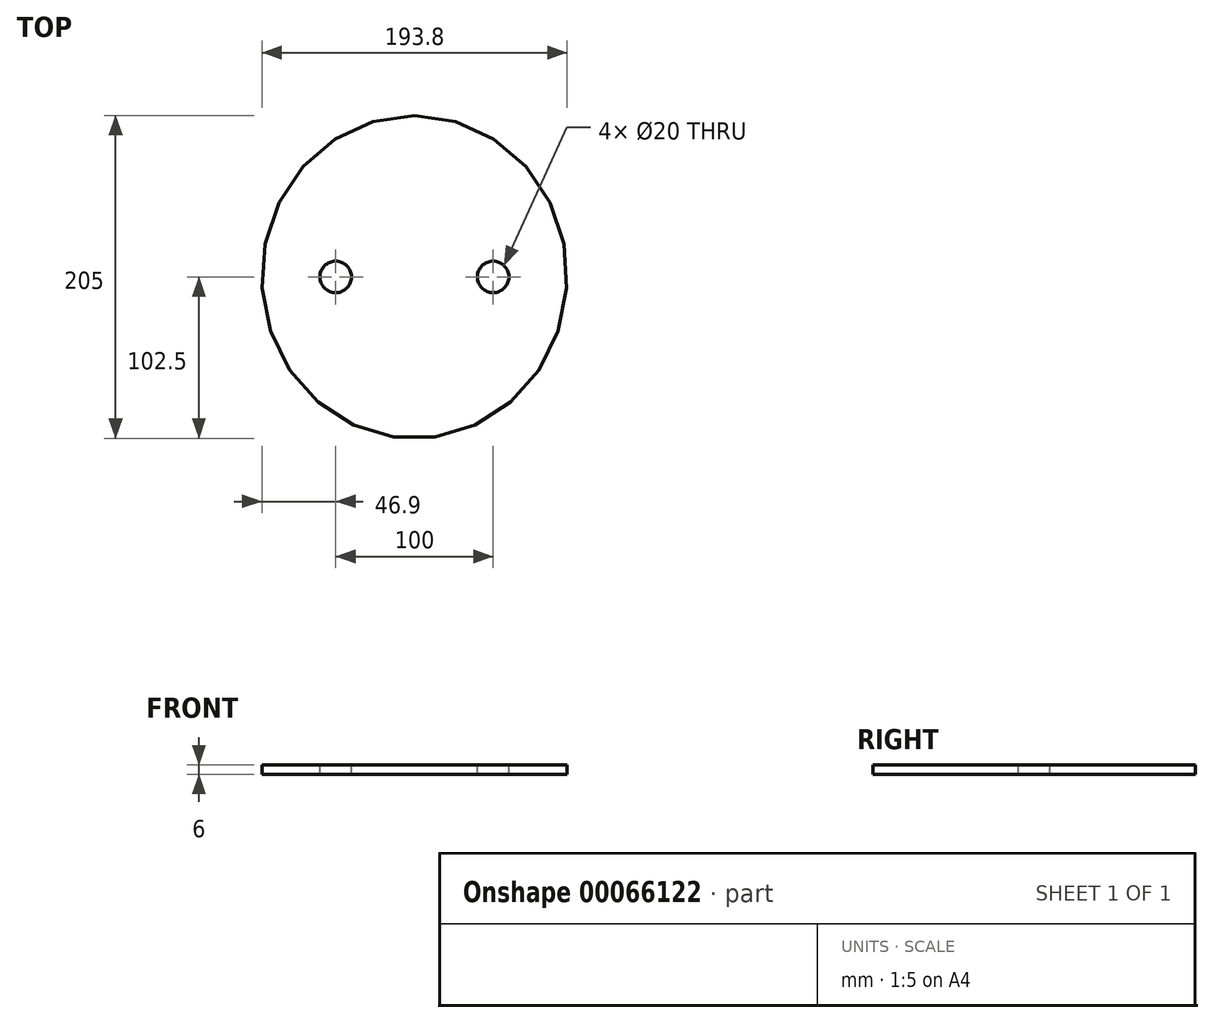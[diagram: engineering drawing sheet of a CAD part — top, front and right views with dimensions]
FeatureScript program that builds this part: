
annotation { "Feature Type Name" : "Feature", "Feature Type Description" : "" }
export const myFeature = defineFeature(function(context is Context, id is Id, definition is map)
    precondition{}
    {
        {
            var Q0;
            Q0=qCreatedBy(makeId("Top.planeOp"),FACE);
            var sketch = newSketch(context, id + "F0", { "sketchPlane" : qUnion([Q0])});
            skEllipse(sketch, "E0", {"center": v(0, 0) * mm, "majorRadius": 102.5 * mm, "minorRadius": 96.9 * mm, "majorAxis": v(0, 1)});
            skLineSegment(sketch, "E1", {"start": v(0, 102.5) * mm, "end": v(0, -102.5) * mm, "construction": true});
            skLineSegment(sketch, "E2", {"start": v(-96.9, 0) * mm, "end": v(96.9, 0) * mm, "construction": true});
            skSolve(sketch);
        }
        {
            var Q0;
            Q0=makeQuery(id+"F0.imprint","IMPRINT",FACE,{"disambiguationData":[TD([[makeQuery(id+"F0.imprint","IMPRINT",EDGE,{"derivedFrom":sQuery(id+"F0.wireOp",EDGE,"E0")}),1.0]])]});
            extrude(context, id + "F1", {"entities" : qUnion([Q0]), "depth" : 6 * mm});
        }
        {
            var Q0;
            Q0=makeQuery(id+"F1.opExtrude","CAP_FACE",FACE,{"disambiguationData":[OSD([sQuery(id+"F0.wireOp",EDGE,"E0")])],"isStart":false});
            var sketch = newSketch(context, id + "F2", { "sketchPlane" : qUnion([Q0])});
            skPoint(sketch, "E3", {"position": v(-50, 0) * mm});
            skPoint(sketch, "E4", {"position": v(50, 0) * mm});
            skSolve(sketch);
        }
        {
            var Q0;
            Q0=sQuery(id+"F2.wireOp",VERTEX,"E3");
            var Q1;
            Q1=sQuery(id+"F2.wireOp",VERTEX,"E4");
            var Q2;
            Q2=makeQuery(id+"F1.opExtrude","SWEPT_BODY",BODY,{"disambiguationData":[OSD([sQuery(id+"F0.wireOp",EDGE,"E0")])]});
            hole(context, id + "F3", {"style" : HoleStyle.SIMPLE, "holeDiameter" : 20 * mm, "endStyle" : HoleEndStyle.THROUGH, "locations" : qUnion([Q0, Q1]), "scope" : qUnion([Q2])});
        }
    });
